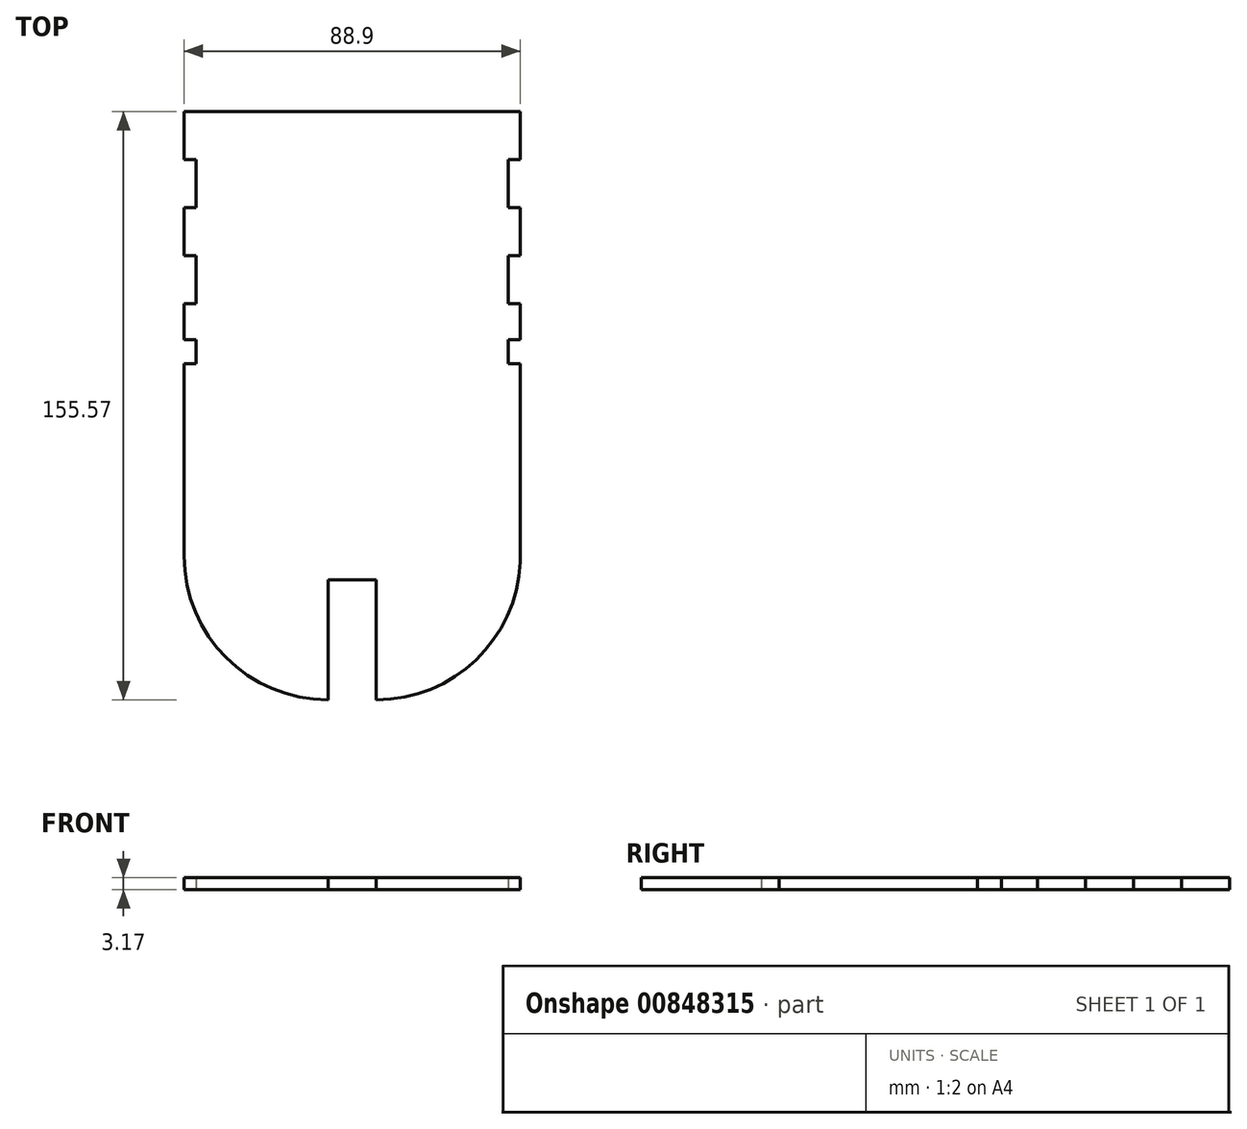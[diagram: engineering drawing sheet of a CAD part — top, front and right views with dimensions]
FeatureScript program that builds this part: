
annotation { "Feature Type Name" : "Feature", "Feature Type Description" : "" }
export const myFeature = defineFeature(function(context is Context, id is Id, definition is map)
    precondition{}
    {
        {
            var Q0;
            Q0=qCreatedBy(makeId("Top.planeOp"),FACE);
            var sketch = newSketch(context, id + "F0", { "sketchPlane" : qUnion([Q0])});
            skPoint(sketch, "E0", {"position": v(-45.33, 18.07) * mm});
            skPoint(sketch, "E1", {"position": v(-45.33, 81.57) * mm});
            skPoint(sketch, "E2", {"position": v(-0.88, 8.55) * mm});
            skPoint(sketch, "E3", {"position": v(43.57, 18.07) * mm});
            skPoint(sketch, "E4", {"position": v(43.57, -74) * mm});
            skLineSegment(sketch, "E5.bottom", {"start": v(-45.33, 81.57) * mm, "end": v(43.57, 81.57) * mm});
            skLineSegment(sketch, "E5.top", {"start": v(-7.23, -74) * mm, "end": v(-7.23, -74) * mm});
            skLineSegment(sketch, "E5.left", {"start": v(-45.33, 81.57) * mm, "end": v(-45.33, 68.87) * mm});
            skLineSegment(sketch, "E5.right", {"start": v(43.57, 81.57) * mm, "end": v(43.57, 68.87) * mm});
            skLineSegment(sketch, "E6", {"start": v(43.57, 68.87) * mm, "end": v(40.4, 68.87) * mm});
            skLineSegment(sketch, "E7", {"start": v(40.4, 68.87) * mm, "end": v(40.4, 56.17) * mm});
            skLineSegment(sketch, "E8", {"start": v(40.4, 56.17) * mm, "end": v(43.57, 56.17) * mm});
            skLineSegment(sketch, "E9", {"start": v(43.57, 43.47) * mm, "end": v(40.4, 43.47) * mm});
            skLineSegment(sketch, "E10", {"start": v(40.4, 43.47) * mm, "end": v(40.4, 30.77) * mm});
            skLineSegment(sketch, "E11", {"start": v(40.4, 30.77) * mm, "end": v(43.57, 30.77) * mm});
            skLineSegment(sketch, "E12", {"start": v(-45.33, 68.87) * mm, "end": v(-42.16, 68.87) * mm});
            skLineSegment(sketch, "E13", {"start": v(-42.16, 68.87) * mm, "end": v(-42.16, 56.17) * mm});
            skLineSegment(sketch, "E14", {"start": v(-42.16, 56.17) * mm, "end": v(-45.33, 56.17) * mm});
            skLineSegment(sketch, "E15", {"start": v(-45.33, 43.47) * mm, "end": v(-42.16, 43.47) * mm});
            skLineSegment(sketch, "E16", {"start": v(-42.16, 43.47) * mm, "end": v(-42.16, 30.77) * mm});
            skLineSegment(sketch, "E17", {"start": v(-42.16, 30.77) * mm, "end": v(-45.33, 30.77) * mm});
            skLineSegment(sketch, "E18", {"start": v(-7.23, -74) * mm, "end": v(-7.23, -42.25) * mm});
            skLineSegment(sketch, "E19", {"start": v(-7.23, -42.25) * mm, "end": v(5.47, -42.25) * mm});
            skLineSegment(sketch, "E20", {"start": v(5.47, -42.25) * mm, "end": v(5.47, -74) * mm});
            skLineSegment(sketch, "E21.trimOffspring", {"start": v(43.57, 30.77) * mm, "end": v(43.57, 21.25) * mm});
            skLineSegment(sketch, "E22.trimOffspring", {"start": v(43.57, 56.17) * mm, "end": v(43.57, 43.47) * mm});
            skLineSegment(sketch, "E23.trimOffspring", {"start": v(-45.33, 56.17) * mm, "end": v(-45.33, 43.47) * mm});
            skLineSegment(sketch, "E24.trimOffspring", {"start": v(-45.33, 30.77) * mm, "end": v(-45.33, 21.25) * mm});
            skLineSegment(sketch, "E25.trimOffspring", {"start": v(5.47, -74) * mm, "end": v(5.5, -74) * mm});
            skPoint(sketch, "E26", {"position": v(43.57, 68.87) * mm});
            skPoint(sketch, "E27.visualSharp", {"position": v(-45.33, -74) * mm});
            skLineSegment(sketch, "E28", {"start": v(43.6, -36.34) * mm, "end": v(43.57, -39.51) * mm});
            skLineSegment(sketch, "E29", {"start": v(-45.33, -39.08) * mm, "end": v(-45.33, -35.9) * mm});
            skPoint(sketch, "E30.visualSharp", {"position": v(-45.33, -32.64) * mm});
            skPoint(sketch, "E31.visualSharp", {"position": v(43.57, -39.3) * mm});
            skArc(sketch, "E31.filletArc", {"start": v(43.57, -39.51) * mm, "mid": v(43.57, -39.3) * mm, "end": v(43.57, -39.08) * mm});
            skArc(sketch, "E32.filletArc", {"start": v(-45.33, -35.9) * mm, "mid": v(-34.17, -62.85) * mm, "end": v(-7.23, -74) * mm});
            skPoint(sketch, "E33.visualSharp", {"position": v(43.17, -74) * mm});
            skArc(sketch, "E33.filletArc", {"start": v(5.5, -74) * mm, "mid": v(32.3, -63) * mm, "end": v(43.6, -36.34) * mm});
            skLineSegment(sketch, "E34", {"start": v(43.57, 21.25) * mm, "end": v(40.4, 21.25) * mm});
            skLineSegment(sketch, "E35", {"start": v(40.4, 21.25) * mm, "end": v(40.4, 14.9) * mm});
            skLineSegment(sketch, "E36", {"start": v(40.4, 14.9) * mm, "end": v(43.57, 14.9) * mm});
            skLineSegment(sketch, "E37.trimOffspring", {"start": v(43.57, 14.9) * mm, "end": v(43.57, -39.08) * mm});
            skLineSegment(sketch, "E38", {"start": v(-45.33, 21.25) * mm, "end": v(-42.16, 21.25) * mm});
            skLineSegment(sketch, "E39", {"start": v(-42.16, 21.25) * mm, "end": v(-42.16, 14.9) * mm});
            skLineSegment(sketch, "E40", {"start": v(-42.16, 14.9) * mm, "end": v(-45.33, 14.9) * mm});
            skLineSegment(sketch, "E41.trimOffspring", {"start": v(-45.33, 14.9) * mm, "end": v(-45.33, -39.08) * mm});
            skSolve(sketch);
        }
        {
            var Q0;
            Q0=makeQuery(id+"F0.imprint","IMPRINT",FACE,{"disambiguationData":[TD([[makeQuery(id+"F0.imprint","IMPRINT",EDGE,{"derivedFrom":sQuery(id+"F0.wireOp",EDGE,"E5.bottom")}),-1.0]])]});
            extrude(context, id + "F1", {"entities" : qUnion([Q0]), "depth" : 3.17 * mm, "offsetDistance" : 25.4 * mm});
        }
    });
